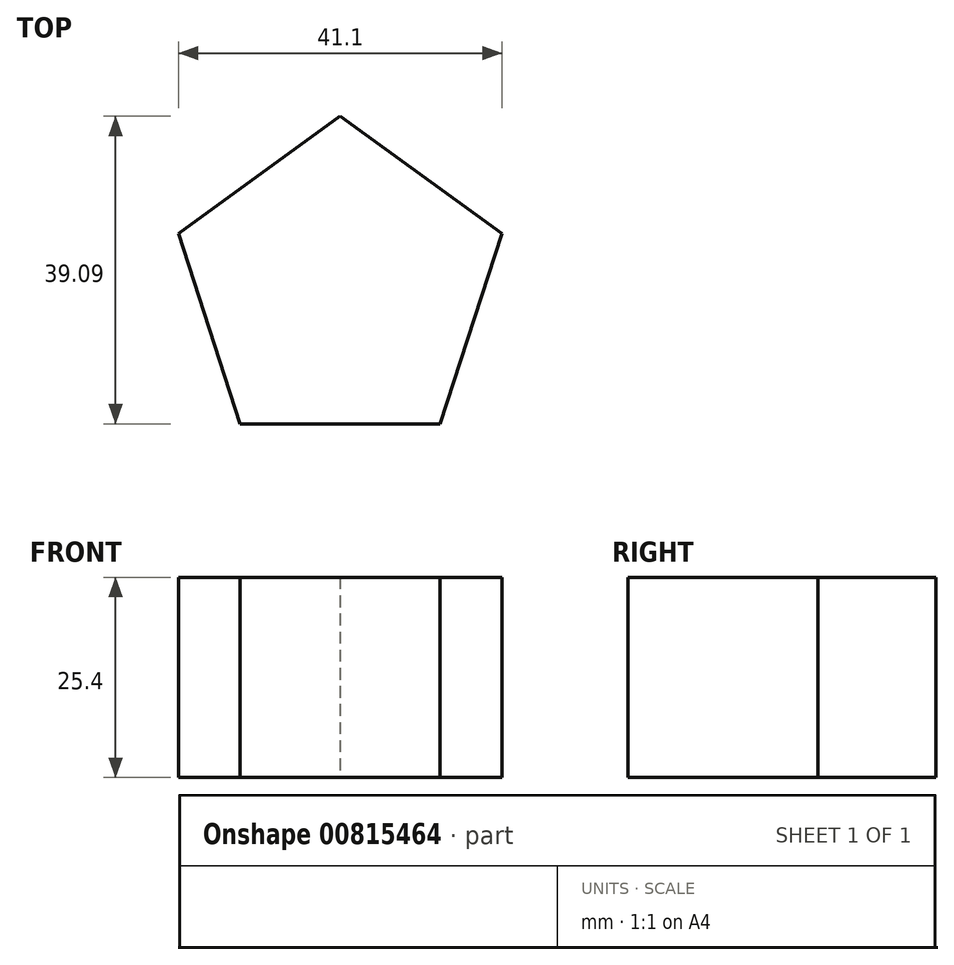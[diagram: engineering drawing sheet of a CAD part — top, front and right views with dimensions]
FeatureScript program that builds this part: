
annotation { "Feature Type Name" : "Feature", "Feature Type Description" : "" }
export const myFeature = defineFeature(function(context is Context, id is Id, definition is map)
    precondition{}
    {
        {
            var Q0;
            Q0=qCreatedBy(makeId("Top.planeOp"),FACE);
            var sketch = newSketch(context, id + "F0", { "sketchPlane" : qUnion([Q0])});
            skCircle(sketch, "E0.cCircle", {"center": v(0, 0) * mm, "radius": 17.48 * mm, "construction": true});
            skLineSegment(sketch, "E0.0", {"start": v(20.55, 6.68) * mm, "end": v(12.7, -17.48) * mm});
            skLineSegment(sketch, "E0.1", {"start": v(12.7, -17.48) * mm, "end": v(-12.7, -17.48) * mm});
            skLineSegment(sketch, "E0.2", {"start": v(-12.7, -17.48) * mm, "end": v(-20.55, 6.68) * mm});
            skLineSegment(sketch, "E0.3", {"start": v(-20.55, 6.68) * mm, "end": v(0, 21.6) * mm});
            skLineSegment(sketch, "E0.4", {"start": v(0, 21.6) * mm, "end": v(20.55, 6.68) * mm});
            skPoint(sketch, "E0.0.midPoint", {"position": v(16.62, -5.4) * mm});
            skPoint(sketch, "E1.0.midPoint", {"position": v(0, 21.6) * mm});
            skSolve(sketch);
        }
        {
            var Q0;
            Q0=makeQuery(id+"F0.imprint","IMPRINT",FACE,{"disambiguationData":[TD([[makeQuery(id+"F0.imprint","IMPRINT",EDGE,{"derivedFrom":sQuery(id+"F0.wireOp",EDGE,"E0.0")}),-1.0]])]});
            extrude(context, id + "F1", {"entities" : qUnion([Q0]), "depth" : 25.4 * mm, "offsetDistance" : 25.4 * mm});
        }
    });
